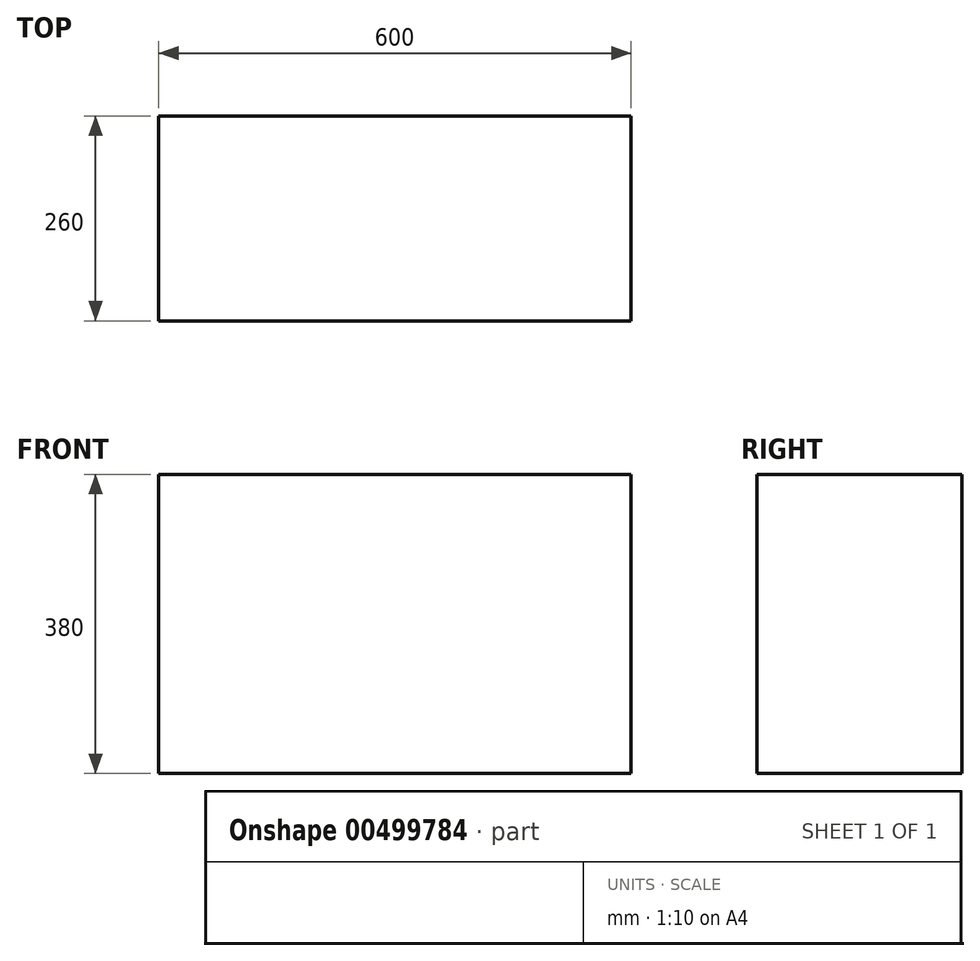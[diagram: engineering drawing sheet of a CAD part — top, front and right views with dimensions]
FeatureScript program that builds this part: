
annotation { "Feature Type Name" : "Feature", "Feature Type Description" : "" }
export const myFeature = defineFeature(function(context is Context, id is Id, definition is map)
    precondition{}
    {
        {
            var Q0;
            Q0=qCreatedBy(makeId("Front.planeOp"),FACE);
            var sketch = newSketch(context, id + "F0", { "sketchPlane" : qUnion([Q0])});
            skLineSegment(sketch, "E0.bottom", {"start": v(290.05, -322.98) * mm, "end": v(-309.95, -322.98) * mm});
            skLineSegment(sketch, "E0.top", {"start": v(290.05, 57.02) * mm, "end": v(-309.95, 57.02) * mm});
            skLineSegment(sketch, "E0.left", {"start": v(290.05, -322.98) * mm, "end": v(290.05, 57.02) * mm});
            skLineSegment(sketch, "E0.right", {"start": v(-309.95, -322.98) * mm, "end": v(-309.95, 57.02) * mm});
            skSolve(sketch);
        }
        {
            var Q0;
            Q0 = qSketchRegion(id + "F0", true);
            extrude(context, id + "F1", {"entities" : qUnion([Q0]), "depth" : 260 * mm});
        }
    });
